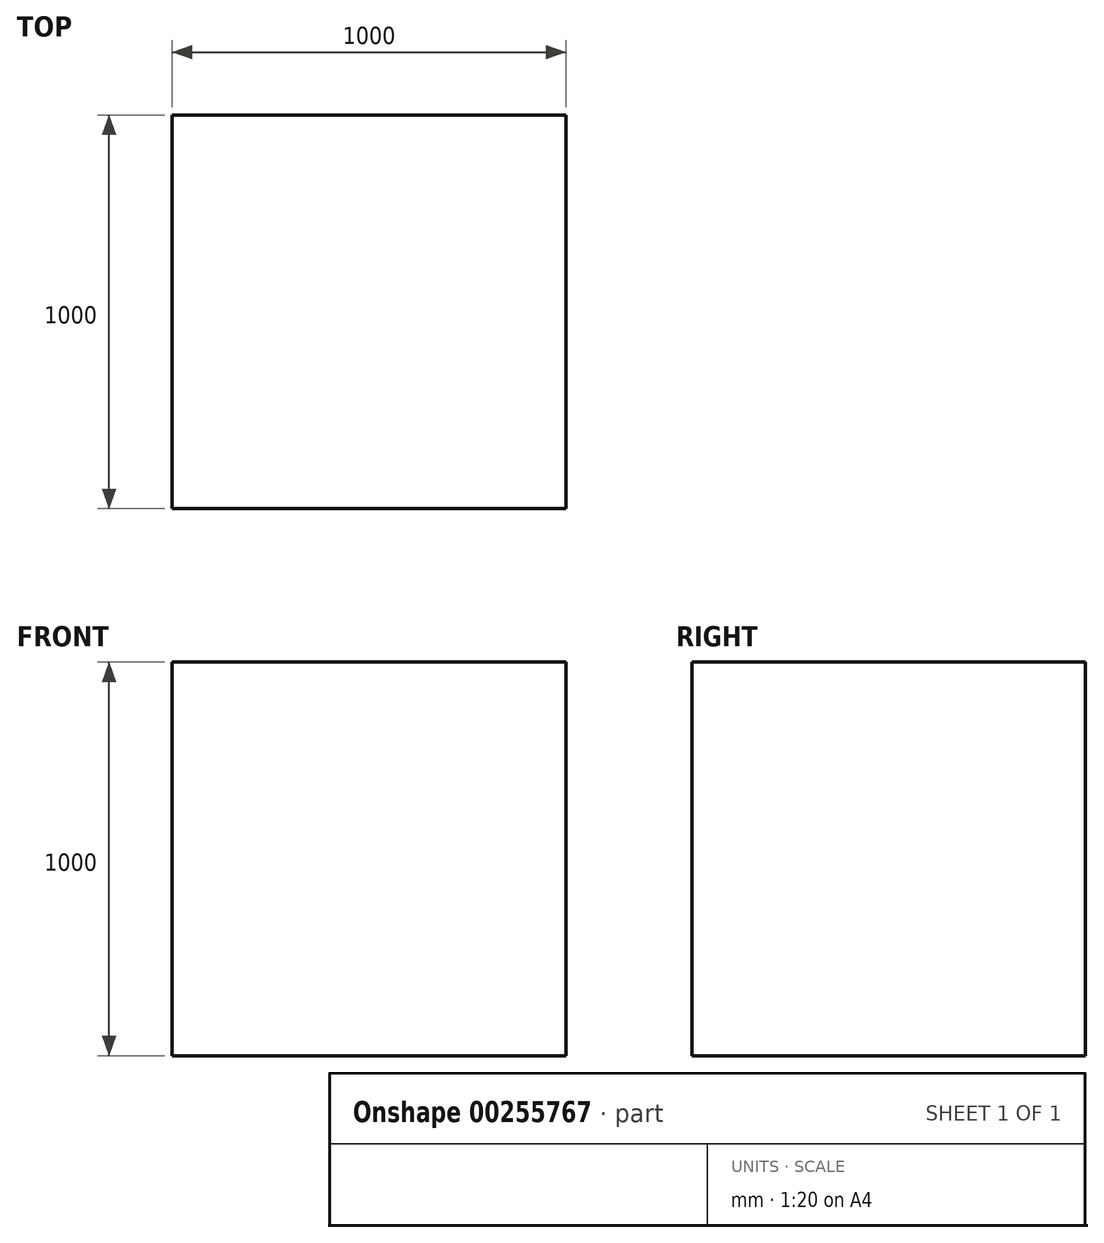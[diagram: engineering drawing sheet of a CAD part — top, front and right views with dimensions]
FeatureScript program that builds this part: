
annotation { "Feature Type Name" : "Feature", "Feature Type Description" : "" }
export const myFeature = defineFeature(function(context is Context, id is Id, definition is map)
    precondition{}
    {
        {
            var Q0;
            Q0=qCreatedBy(makeId("Front.planeOp"),FACE);
            var sketch = newSketch(context, id + "F0", { "sketchPlane" : qUnion([Q0])});
            skLineSegment(sketch, "E0.bottom", {"start": v(0, 0) * mm, "end": v(1000, 0) * mm});
            skLineSegment(sketch, "E0.top", {"start": v(0, 1000) * mm, "end": v(1000, 1000) * mm});
            skLineSegment(sketch, "E0.left", {"start": v(0, 0) * mm, "end": v(0, 1000) * mm});
            skLineSegment(sketch, "E0.right", {"start": v(1000, 0) * mm, "end": v(1000, 1000) * mm});
            skSolve(sketch);
        }
        {
            var Q0;
            Q0 = qSketchRegion(id + "F0", true);
            extrude(context, id + "F1", {"entities" : qUnion([Q0]), "oppositeDirection" : true, "depth" : 1000 * mm, "offsetDistance" : 25 * mm});
        }
    });
